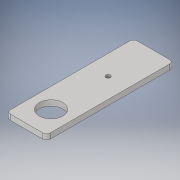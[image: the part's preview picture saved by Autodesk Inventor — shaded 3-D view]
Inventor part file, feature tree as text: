
AUTODESK INVENTOR PART (.ipt)
format: ipt  version: 2019 (Build 230136000, 136)  size: 110,592 bytes
history: native  units: mm
features: extrude x1, sketch x1
ambient origin geometry x8: Origin, YZ Plane, XZ Plane, XY Plane, X Axis, Y Axis, Z Axis, Center Point
bodies: Solid1 (feature_tree)
feature tree (2):
  extrude  "Extrusion1"  Depth=70.0mm
  sketch  "Sketch1"  dims[d0=22.0mm d1=70.0mm d2=2.5mm d3=25.0mm d6=11.0mm d8=2.0mm d9=13.0mm d10=31.5mm d11=3.0mm d12=0.0mm]
